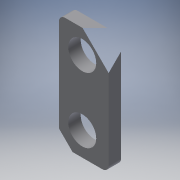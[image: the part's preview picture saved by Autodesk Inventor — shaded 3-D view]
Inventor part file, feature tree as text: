
AUTODESK INVENTOR PART (.ipt)
format: ipt  version: 2016 (Build 200138000, 138)  size: 114,176 bytes
history: native  units: in
note: dims shown in document units (in); Inventor stores cm internally (conversion verified against a paired STEP export)
features: reference x2, extrude x1, fillet x1, sketch x1
ambient origin geometry x8: Origin, YZ Plane, XZ Plane, XY Plane, X Axis, Y Axis, Z Axis, Center Point
bodies: Solid1 (feature_tree)
feature tree (5):
  extrude  "Extrusion1"  Depth=0.0394in
  fillet  "Fillet1"  Radius=0.0787in
  sketch  "Sketch1"  dims[d0=0.1772in d1=0.1772in d2=0.0787in d3=0.315in d4=0.0787in d5=0.0in d6=0.0394in]
  reference  "Reference1"
  reference  "Reference2"
